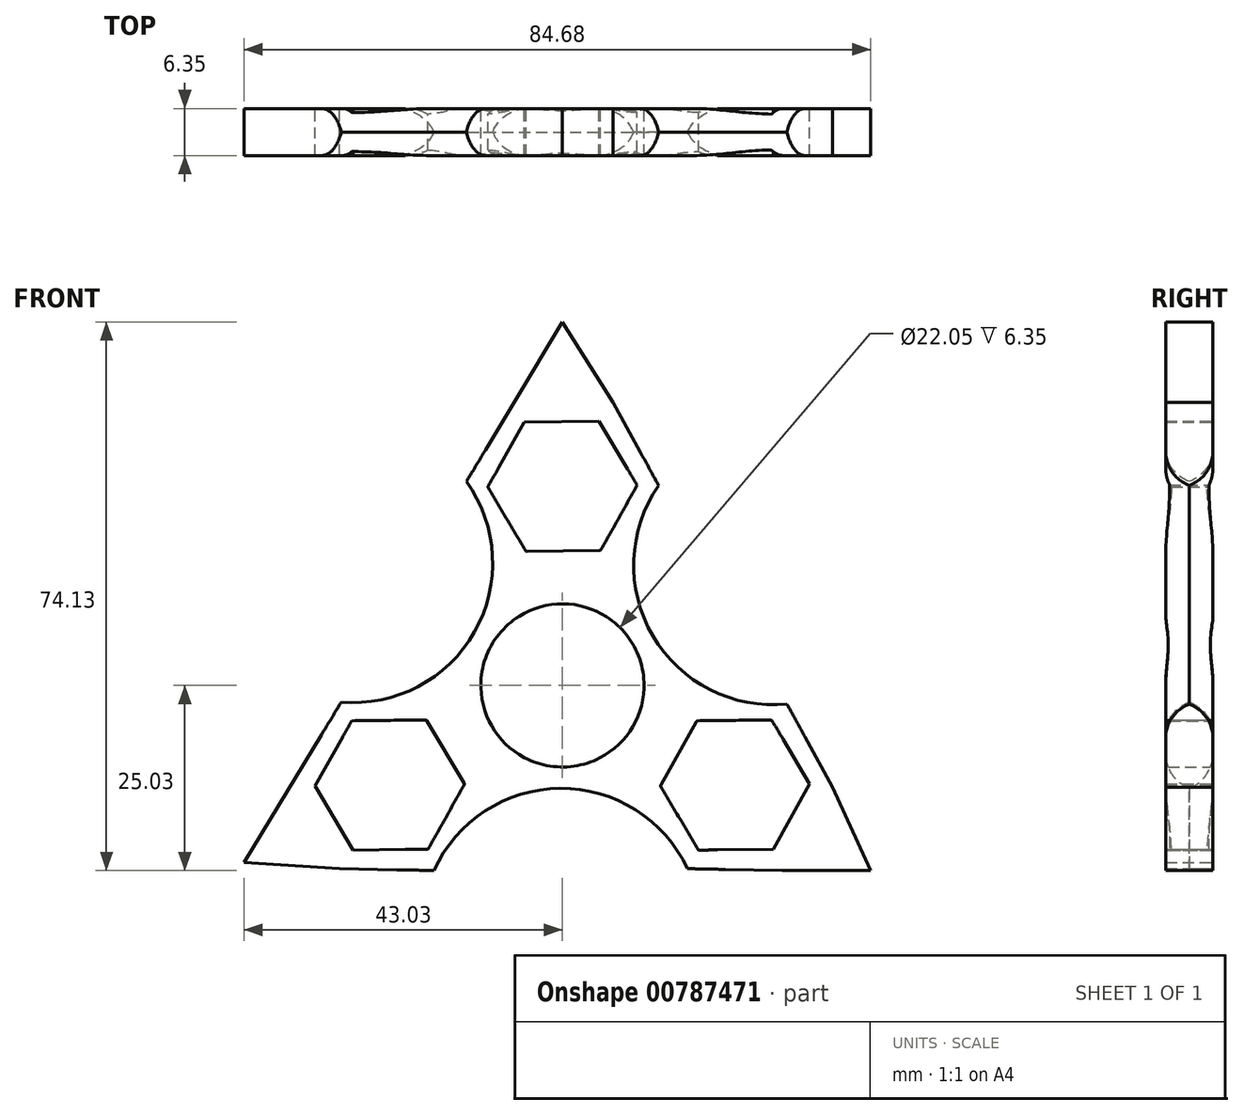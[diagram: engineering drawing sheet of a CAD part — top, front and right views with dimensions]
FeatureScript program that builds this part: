
annotation { "Feature Type Name" : "Feature", "Feature Type Description" : "" }
export const myFeature = defineFeature(function(context is Context, id is Id, definition is map)
    precondition{}
    {
        {
            var Q0;
            Q0=qCreatedBy(makeId("Front.planeOp"),FACE);
            var sketch = newSketch(context, id + "F0", { "sketchPlane" : qUnion([Q0])});
            skCircle(sketch, "E0", {"center": v(0, 0) * mm, "radius": 11.02 * mm});
            skCircle(sketch, "E1", {"center": v(0, 0) * mm, "radius": 14.29 * mm});
            skCircle(sketch, "E2.cCircle", {"center": v(0, 26.92) * mm, "radius": 8.74 * mm, "construction": true});
            skLineSegment(sketch, "E2.0", {"start": v(4.94, 35.72) * mm, "end": v(10.09, 27.05) * mm});
            skLineSegment(sketch, "E2.1", {"start": v(10.09, 27.05) * mm, "end": v(5.15, 18.25) * mm});
            skLineSegment(sketch, "E2.2", {"start": v(5.15, 18.25) * mm, "end": v(-4.94, 18.12) * mm});
            skLineSegment(sketch, "E2.3", {"start": v(-4.94, 18.12) * mm, "end": v(-10.09, 26.8) * mm});
            skLineSegment(sketch, "E2.4", {"start": v(-10.09, 26.8) * mm, "end": v(-5.15, 35.6) * mm});
            skLineSegment(sketch, "E2.5", {"start": v(-5.15, 35.6) * mm, "end": v(4.94, 35.72) * mm});
            skPoint(sketch, "E2.0.midPoint", {"position": v(7.51, 31.38) * mm});
            skCircle(sketch, "E3.cCircle", {"center": v(0, 26.92) * mm, "radius": 11.43 * mm, "construction": true});
            skLineSegment(sketch, "E3.0", {"start": v(-13.2, 27.2) * mm, "end": v(-6.36, 38.49) * mm});
            skLineSegment(sketch, "E3.1", {"start": v(-6.36, 38.49) * mm, "end": v(6.83, 38.21) * mm});
            skLineSegment(sketch, "E3.2", {"start": v(6.83, 38.21) * mm, "end": v(13.2, 26.65) * mm});
            skLineSegment(sketch, "E3.3", {"start": v(13.2, 26.65) * mm, "end": v(6.36, 15.36) * mm});
            skLineSegment(sketch, "E3.4", {"start": v(6.36, 15.36) * mm, "end": v(-6.83, 15.63) * mm});
            skLineSegment(sketch, "E3.5", {"start": v(-6.83, 15.63) * mm, "end": v(-13.2, 27.2) * mm});
            skPoint(sketch, "E3.0.midPoint", {"position": v(-9.78, 32.84) * mm});
            skLineSegment(sketch, "E4.1.0", {"start": v(-29.68, -1.9) * mm, "end": v(-16.48, -2.17) * mm});
            skCircle(sketch, "E4.1.1", {"center": v(-23.32, -13.46) * mm, "radius": 11.43 * mm, "construction": true});
            skLineSegment(sketch, "E4.1.2", {"start": v(-10.12, -13.73) * mm, "end": v(-16.95, -25.03) * mm});
            skLineSegment(sketch, "E4.1.3", {"start": v(-16.48, -2.17) * mm, "end": v(-10.12, -13.73) * mm});
            skLineSegment(sketch, "E4.1.4", {"start": v(-36.51, -13.19) * mm, "end": v(-29.68, -1.9) * mm});
            skLineSegment(sketch, "E4.1.5", {"start": v(-30.15, -24.75) * mm, "end": v(-36.51, -13.19) * mm});
            skLineSegment(sketch, "E4.1.6", {"start": v(-16.95, -25.03) * mm, "end": v(-30.15, -24.75) * mm});
            skLineSegment(sketch, "E4.1.7", {"start": v(-18.16, -22.14) * mm, "end": v(-28.25, -22.26) * mm});
            skLineSegment(sketch, "E4.1.8", {"start": v(-13.23, -13.34) * mm, "end": v(-18.16, -22.14) * mm});
            skCircle(sketch, "E4.1.9", {"center": v(-23.32, -13.46) * mm, "radius": 8.74 * mm, "construction": true});
            skLineSegment(sketch, "E4.1.10", {"start": v(-18.38, -4.66) * mm, "end": v(-13.23, -13.34) * mm});
            skLineSegment(sketch, "E4.1.11", {"start": v(-28.47, -4.79) * mm, "end": v(-18.38, -4.66) * mm});
            skLineSegment(sketch, "E4.1.12", {"start": v(-33.4, -13.58) * mm, "end": v(-28.47, -4.79) * mm});
            skLineSegment(sketch, "E4.1.13", {"start": v(-28.25, -22.26) * mm, "end": v(-33.4, -13.58) * mm});
            skLineSegment(sketch, "E4.2.0", {"start": v(16.48, -24.75) * mm, "end": v(10.12, -13.19) * mm});
            skCircle(sketch, "E4.2.1", {"center": v(23.32, -13.46) * mm, "radius": 11.43 * mm, "construction": true});
            skLineSegment(sketch, "E4.2.2", {"start": v(16.95, -1.9) * mm, "end": v(30.15, -2.17) * mm});
            skLineSegment(sketch, "E4.2.3", {"start": v(10.12, -13.19) * mm, "end": v(16.95, -1.9) * mm});
            skLineSegment(sketch, "E4.2.4", {"start": v(29.68, -25.03) * mm, "end": v(16.48, -24.75) * mm});
            skLineSegment(sketch, "E4.2.5", {"start": v(36.51, -13.73) * mm, "end": v(29.68, -25.03) * mm});
            skLineSegment(sketch, "E4.2.6", {"start": v(30.15, -2.17) * mm, "end": v(36.51, -13.73) * mm});
            skLineSegment(sketch, "E4.2.7", {"start": v(28.25, -4.66) * mm, "end": v(33.4, -13.34) * mm});
            skLineSegment(sketch, "E4.2.8", {"start": v(18.16, -4.79) * mm, "end": v(28.25, -4.66) * mm});
            skCircle(sketch, "E4.2.9", {"center": v(23.32, -13.46) * mm, "radius": 8.74 * mm, "construction": true});
            skLineSegment(sketch, "E4.2.10", {"start": v(13.23, -13.58) * mm, "end": v(18.16, -4.79) * mm});
            skLineSegment(sketch, "E4.2.11", {"start": v(18.38, -22.26) * mm, "end": v(13.23, -13.58) * mm});
            skLineSegment(sketch, "E4.2.12", {"start": v(28.47, -22.14) * mm, "end": v(18.38, -22.26) * mm});
            skLineSegment(sketch, "E4.2.13", {"start": v(33.4, -13.34) * mm, "end": v(28.47, -22.14) * mm});
            skArc(sketch, "E5", {"start": v(-29.68, -1.9) * mm, "mid": v(-12.2, 7.42) * mm, "end": v(-13.2, 27.2) * mm});
            skArc(sketch, "E6", {"start": v(13.2, 26.65) * mm, "mid": v(12.54, 6.87) * mm, "end": v(30.15, -2.17) * mm});
            skArc(sketch, "E7", {"start": v(16.48, -24.75) * mm, "mid": v(-0.32, -14.29) * mm, "end": v(-16.95, -25.03) * mm});
            skLineSegment(sketch, "E8", {"start": v(-36.51, -13.19) * mm, "end": v(-43.03, -23.95) * mm});
            skLineSegment(sketch, "E9", {"start": v(-43.03, -23.95) * mm, "end": v(-30.15, -24.75) * mm});
            skLineSegment(sketch, "E10", {"start": v(41.65, -25.03) * mm, "end": v(36.51, -13.73) * mm});
            skLineSegment(sketch, "E11", {"start": v(41.65, -25.03) * mm, "end": v(29.68, -25.03) * mm});
            skArc(sketch, "E12", {"start": v(-29.68, -1.9) * mm, "mid": v(-36.35, -5.57) * mm, "end": v(-36.51, -13.19) * mm});
            skArc(sketch, "E13", {"start": v(-30.15, -24.75) * mm, "mid": v(-23.63, -28.7) * mm, "end": v(-16.95, -25.03) * mm});
            skArc(sketch, "E14", {"start": v(16.48, -24.75) * mm, "mid": v(23, -28.7) * mm, "end": v(29.68, -25.03) * mm});
            skArc(sketch, "E15", {"start": v(36.51, -13.73) * mm, "mid": v(36.67, -6.12) * mm, "end": v(30.15, -2.17) * mm});
            skArc(sketch, "E16", {"start": v(13.2, 26.65) * mm, "mid": v(13.35, 34.27) * mm, "end": v(6.83, 38.21) * mm});
            skArc(sketch, "E17", {"start": v(-6.36, 38.49) * mm, "mid": v(-13.04, 34.81) * mm, "end": v(-13.2, 27.2) * mm});
            skLineSegment(sketch, "E18", {"start": v(-6.36, 38.49) * mm, "end": v(0, 49.1) * mm});
            skLineSegment(sketch, "E19", {"start": v(0, 49.1) * mm, "end": v(6.83, 38.21) * mm});
            skSolve(sketch);
        }
        {
            var Q0;
            Q0=makeQuery(id+"F0.imprint","IMPRINT",FACE,{"disambiguationData":[TD([[makeQuery(id+"F0.imprint","IMPRINT",EDGE,{"derivedFrom":sQuery(id+"F0.wireOp",EDGE,"E3.0")}),1.0]])]});
            var Q1;
            Q1=makeQuery(id+"F0.imprint","IMPRINT",FACE,{"disambiguationData":[TD([[makeQuery(id+"F0.imprint","IMPRINT",EDGE,{"derivedFrom":sQuery(id+"F0.wireOp",EDGE,"E2.0")}),1.0]])]});
            var Q2;
            Q2=makeQuery(id+"F0.imprint","IMPRINT",FACE,{"disambiguationData":[TD([[makeQuery(id+"F0.imprint","IMPRINT",EDGE,{"derivedFrom":sQuery(id+"F0.wireOp",EDGE,"E3.1")}),1.0]])]});
            var Q3;
            Q3=makeQuery(id+"F0.imprint","IMPRINT",FACE,{"disambiguationData":[TD([[makeQuery(id+"F0.imprint","IMPRINT",EDGE,{"derivedFrom":sQuery(id+"F0.wireOp",EDGE,"E3.2")}),1.0]])]});
            var Q4;
            {var subQ1=sQuery(id+"F0.wireOp",EDGE,"E3.4");Q4=makeQuery(id+"F0.imprint","IMPRINT",FACE,{"disambiguationData":[TD([[makeQuery(id+"F0.imprint","IMPRINT",EDGE,{"derivedFrom":subQ1}),1.0]])]});}
            var Q5;
            {var subQ0=sQuery(id+"F0.wireOp",EDGE,"E4.1.3");Q5=makeQuery(id+"F0.imprint","IMPRINT",FACE,{"disambiguationData":[TD([[makeQuery(id+"F0.imprint","IMPRINT",EDGE,{"derivedFrom":subQ0}),1.0]])]});}
            var Q6;
            {var subQ1=sQuery(id+"F0.wireOp",EDGE,"E4.1.3");Q6=makeQuery(id+"F0.imprint","IMPRINT",FACE,{"disambiguationData":[TD([[makeQuery(id+"F0.imprint","IMPRINT",EDGE,{"derivedFrom":subQ1}),-1.0]])]});}
            var Q7;
            Q7=makeQuery(id+"F0.imprint","IMPRINT",FACE,{"disambiguationData":[TD([[makeQuery(id+"F0.imprint","IMPRINT",EDGE,{"derivedFrom":sQuery(id+"F0.wireOp",EDGE,"E4.1.4")}),1.0]])]});
            var Q8;
            Q8=makeQuery(id+"F0.imprint","IMPRINT",FACE,{"disambiguationData":[TD([[makeQuery(id+"F0.imprint","IMPRINT",EDGE,{"derivedFrom":sQuery(id+"F0.wireOp",EDGE,"E4.1.5")}),1.0]])]});
            var Q9;
            Q9=makeQuery(id+"F0.imprint","IMPRINT",FACE,{"disambiguationData":[TD([[makeQuery(id+"F0.imprint","IMPRINT",EDGE,{"derivedFrom":sQuery(id+"F0.wireOp",EDGE,"E4.1.6")}),1.0]])]});
            var Q10;
            Q10=makeQuery(id+"F0.imprint","IMPRINT",FACE,{"disambiguationData":[TD([[makeQuery(id+"F0.imprint","IMPRINT",EDGE,{"derivedFrom":sQuery(id+"F0.wireOp",EDGE,"E4.2.4")}),1.0]])]});
            var Q11;
            Q11=makeQuery(id+"F0.imprint","IMPRINT",FACE,{"disambiguationData":[TD([[makeQuery(id+"F0.imprint","IMPRINT",EDGE,{"derivedFrom":sQuery(id+"F0.wireOp",EDGE,"E4.2.5")}),1.0]])]});
            var Q12;
            {var subQ1=sQuery(id+"F0.wireOp",EDGE,"E4.2.3");Q12=makeQuery(id+"F0.imprint","IMPRINT",FACE,{"disambiguationData":[TD([[makeQuery(id+"F0.imprint","IMPRINT",EDGE,{"derivedFrom":subQ1}),-1.0]])]});}
            var Q13;
            Q13=makeQuery(id+"F0.imprint","IMPRINT",FACE,{"disambiguationData":[TD([[makeQuery(id+"F0.imprint","IMPRINT",EDGE,{"derivedFrom":sQuery(id+"F0.wireOp",EDGE,"E4.2.6")}),1.0]])]});
            var Q14;
            Q14=makeQuery(id+"F0.imprint","IMPRINT",FACE,{"disambiguationData":[TD([[makeQuery(id+"F0.imprint","IMPRINT",EDGE,{"derivedFrom":sQuery(id+"F0.wireOp",EDGE,"E0")}),-1.0]])]});
            extrude(context, id + "F1", {"entities" : qUnion([Q0, Q1, Q2, Q3, Q4, Q5, Q6, Q7, Q8, Q9, Q10, Q11, Q12, Q13, Q14]), "depth" : 6.35 * mm, "offsetDistance" : 25.4 * mm});
        }
        {
            var Q0;
            Q0=makeQuery(id+"F1.opExtrude","CAP_FACE",FACE,{"disambiguationData":[OSD([sQuery(id+"F0.wireOp",EDGE,"E0"),sQuery(id+"F0.wireOp",EDGE,"E2.0"),sQuery(id+"F0.wireOp",EDGE,"E2.1"),sQuery(id+"F0.wireOp",EDGE,"E2.2"),sQuery(id+"F0.wireOp",EDGE,"E2.3"),sQuery(id+"F0.wireOp",EDGE,"E2.4"),sQuery(id+"F0.wireOp",EDGE,"E2.5"),sQuery(id+"F0.wireOp",EDGE,"E4.1.7"),sQuery(id+"F0.wireOp",EDGE,"E4.1.8"),sQuery(id+"F0.wireOp",EDGE,"E4.1.10"),sQuery(id+"F0.wireOp",EDGE,"E4.1.11"),sQuery(id+"F0.wireOp",EDGE,"E4.1.12"),sQuery(id+"F0.wireOp",EDGE,"E4.1.13"),sQuery(id+"F0.wireOp",EDGE,"E4.2.7"),sQuery(id+"F0.wireOp",EDGE,"E4.2.8"),sQuery(id+"F0.wireOp",EDGE,"E4.2.10"),sQuery(id+"F0.wireOp",EDGE,"E4.2.11"),sQuery(id+"F0.wireOp",EDGE,"E4.2.12"),sQuery(id+"F0.wireOp",EDGE,"E4.2.13"),sQuery(id+"F0.wireOp",EDGE,"E5"),sQuery(id+"F0.wireOp",EDGE,"E6"),sQuery(id+"F0.wireOp",EDGE,"E7"),sQuery(id+"F0.wireOp",EDGE,"E8"),sQuery(id+"F0.wireOp",EDGE,"E9"),sQuery(id+"F0.wireOp",EDGE,"E10"),sQuery(id+"F0.wireOp",EDGE,"E11"),sQuery(id+"F0.wireOp",EDGE,"E12"),sQuery(id+"F0.wireOp",EDGE,"E13"),sQuery(id+"F0.wireOp",EDGE,"E14"),sQuery(id+"F0.wireOp",EDGE,"E15"),sQuery(id+"F0.wireOp",EDGE,"E16"),sQuery(id+"F0.wireOp",EDGE,"E17"),sQuery(id+"F0.wireOp",EDGE,"E18"),sQuery(id+"F0.wireOp",EDGE,"E19")])],"isStart":false});
            var sketch = newSketch(context, id + "F2", { "sketchPlane" : qUnion([Q0])});
            skLineSegment(sketch, "E20", {"start": v(-30.15, -24.75) * mm, "end": v(-16.95, -25.03) * mm});
            skLineSegment(sketch, "E21", {"start": v(-36.51, -13.19) * mm, "end": v(-29.68, -1.9) * mm});
            skLineSegment(sketch, "E22", {"start": v(16.48, -24.75) * mm, "end": v(29.68, -25.03) * mm});
            skLineSegment(sketch, "E23", {"start": v(-13.2, 27.2) * mm, "end": v(-6.36, 38.49) * mm});
            skLineSegment(sketch, "E24", {"start": v(36.51, -13.73) * mm, "end": v(30.15, -2.17) * mm});
            skLineSegment(sketch, "E25", {"start": v(13.2, 26.65) * mm, "end": v(6.83, 38.21) * mm});
            skSolve(sketch);
        }
        {
            var Q0;
            Q0=makeQuery(id+"F2.imprint","IMPRINT",FACE,{"disambiguationData":[TD([[makeQuery(id+"F2.imprint","IMPRINT",EDGE,{"derivedFrom":sQuery(id+"F2.wireOp",EDGE,"E20")}),-1.0]])]});
            var Q1;
            Q1=makeQuery(id+"F2.imprint","IMPRINT",FACE,{"disambiguationData":[TD([[makeQuery(id+"F2.imprint","IMPRINT",EDGE,{"derivedFrom":sQuery(id+"F2.wireOp",EDGE,"E21")}),1.0]])]});
            var Q2;
            Q2=makeQuery(id+"F2.imprint","IMPRINT",FACE,{"disambiguationData":[TD([[makeQuery(id+"F2.imprint","IMPRINT",EDGE,{"derivedFrom":sQuery(id+"F2.wireOp",EDGE,"E24")}),-1.0]])]});
            var Q3;
            Q3=makeQuery(id+"F2.imprint","IMPRINT",FACE,{"disambiguationData":[TD([[makeQuery(id+"F2.imprint","IMPRINT",EDGE,{"derivedFrom":sQuery(id+"F2.wireOp",EDGE,"E22")}),-1.0]])]});
            var Q4;
            Q4=makeQuery(id+"F2.imprint","IMPRINT",FACE,{"disambiguationData":[TD([[makeQuery(id+"F2.imprint","IMPRINT",EDGE,{"derivedFrom":sQuery(id+"F2.wireOp",EDGE,"E25")}),-1.0]])]});
            var Q5;
            Q5=makeQuery(id+"F2.imprint","IMPRINT",FACE,{"disambiguationData":[TD([[makeQuery(id+"F2.imprint","IMPRINT",EDGE,{"derivedFrom":sQuery(id+"F2.wireOp",EDGE,"E23")}),1.0]])]});
            extrude(context, id + "F3", {"entities" : qUnion([Q0, Q1, Q2, Q3, Q4, Q5]), "operationType" : NewBodyOperationType.REMOVE, "endBound" : BoundingType.THROUGH_ALL, "oppositeDirection" : true, "depth" : 25.4 * mm, "offsetDistance" : 25.4 * mm});
        }
        {
            var Q0;
            Q0=makeQuery(id+"F1.opExtrude","CAP_EDGE",EDGE,{"disambiguationData":[OSD([sQuery(id+"F0.wireOp",EDGE,"E5")])],"isStart":false});
            var Q1;
            Q1=makeQuery(id+"F1.opExtrude","CAP_EDGE",EDGE,{"disambiguationData":[OSD([sQuery(id+"F0.wireOp",EDGE,"E5")])],"isStart":true});
            fillet(context, id + "F4", {"entities" : qUnion([Q0, Q1]), "radius" : 5.08 * mm, "tangentPropagation" : true, "allowEdgeOverflow" : false});
        }
        {
            var Q0;
            Q0=makeQuery(id+"F1.opExtrude","CAP_EDGE",EDGE,{"disambiguationData":[OSD([sQuery(id+"F0.wireOp",EDGE,"E6")])],"isStart":false});
            var Q1;
            Q1=makeQuery(id+"F1.opExtrude","CAP_EDGE",EDGE,{"disambiguationData":[OSD([sQuery(id+"F0.wireOp",EDGE,"E6")])],"isStart":true});
            var Q2;
            Q2=makeQuery(id+"F1.opExtrude","CAP_EDGE",EDGE,{"disambiguationData":[OSD([sQuery(id+"F0.wireOp",EDGE,"E7")])],"isStart":true});
            var Q3;
            Q3=makeQuery(id+"F1.opExtrude","CAP_EDGE",EDGE,{"disambiguationData":[OSD([sQuery(id+"F0.wireOp",EDGE,"E7")])],"isStart":false});
            fillet(context, id + "F5", {"entities" : qUnion([Q0, Q1, Q2, Q3]), "radius" : 5.08 * mm, "tangentPropagation" : true, "allowEdgeOverflow" : false});
        }
    });
